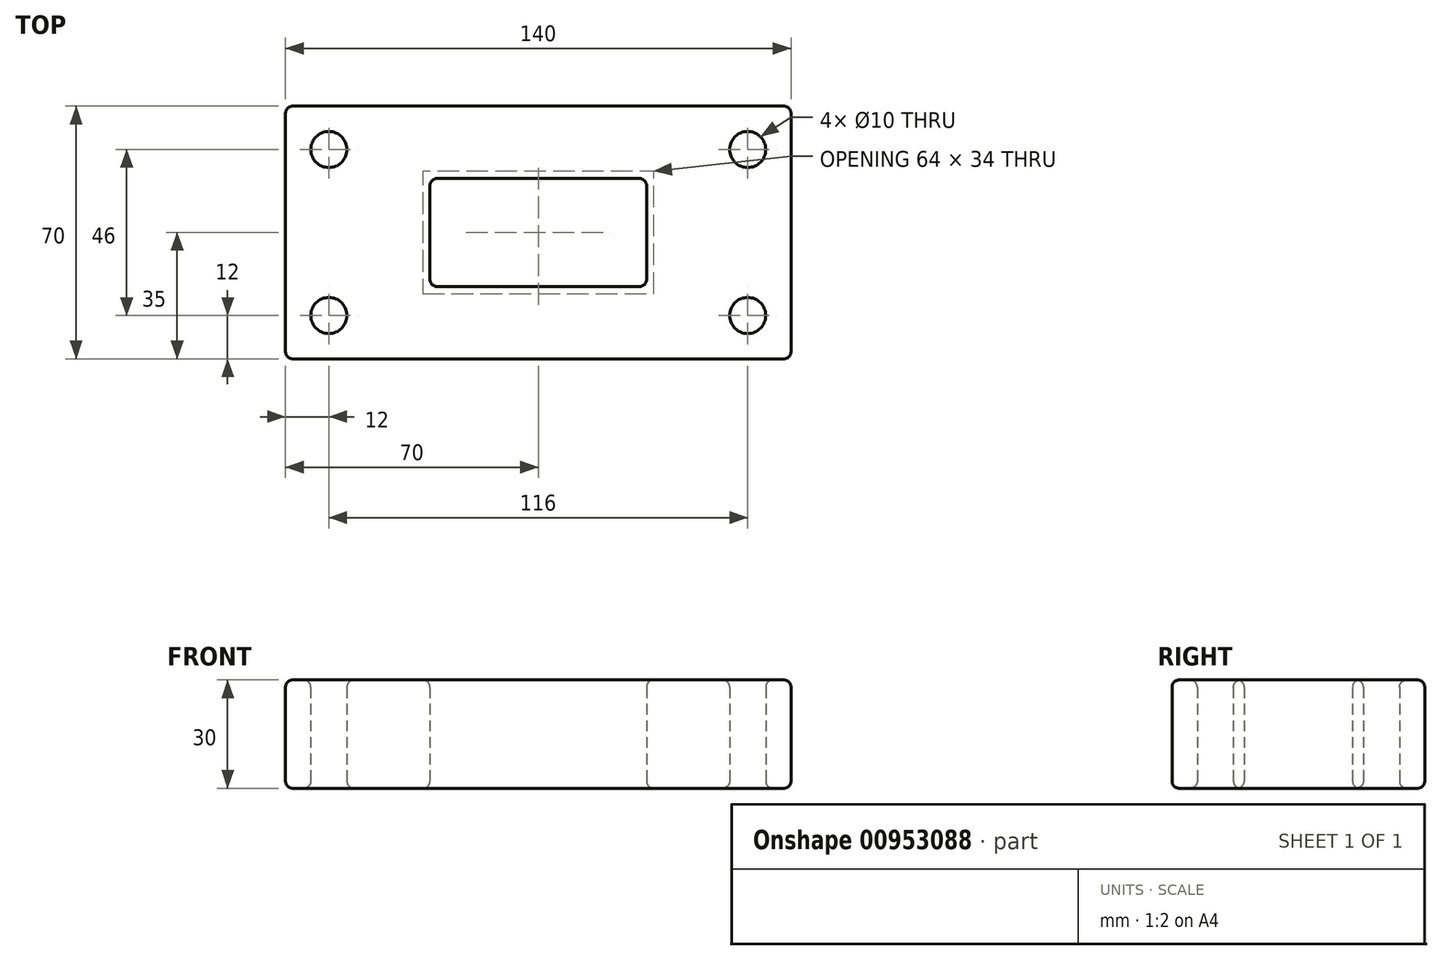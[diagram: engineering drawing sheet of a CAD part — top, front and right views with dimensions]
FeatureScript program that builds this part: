
annotation { "Feature Type Name" : "Feature", "Feature Type Description" : "" }
export const myFeature = defineFeature(function(context is Context, id is Id, definition is map)
    precondition{}
    {
        {
            var Q0;
            Q0=qCreatedBy(makeId("Top.planeOp"),FACE);
            var sketch = newSketch(context, id + "F0", { "sketchPlane" : qUnion([Q0])});
            skLineSegment(sketch, "E0", {"start": v(0, 118.1) * mm, "end": v(0, -115.12) * mm, "construction": true});
            skLineSegment(sketch, "E1", {"start": v(-191.06, 0) * mm, "end": v(202.57, 0) * mm, "construction": true});
            skLineSegment(sketch, "E2.bottom", {"start": v(-70, 35) * mm, "end": v(70, 35) * mm});
            skLineSegment(sketch, "E2.top", {"start": v(-70, -35) * mm, "end": v(70, -35) * mm});
            skLineSegment(sketch, "E2.left", {"start": v(-70, 35) * mm, "end": v(-70, -35) * mm});
            skLineSegment(sketch, "E2.right", {"start": v(70, 35) * mm, "end": v(70, -35) * mm});
            skPoint(sketch, "E2.middle", {"position": v(0, 0) * mm});
            skLineSegment(sketch, "E3.bottom", {"start": v(-30, 15) * mm, "end": v(30, 15) * mm});
            skLineSegment(sketch, "E3.top", {"start": v(-30, -15) * mm, "end": v(30, -15) * mm});
            skLineSegment(sketch, "E3.left", {"start": v(-30, 15) * mm, "end": v(-30, -15) * mm});
            skLineSegment(sketch, "E3.right", {"start": v(30, 15) * mm, "end": v(30, -15) * mm});
            skCircle(sketch, "E4", {"center": v(-58, 23) * mm, "radius": 5 * mm});
            skCircle(sketch, "E5", {"center": v(58, 23) * mm, "radius": 5 * mm});
            skCircle(sketch, "E6.MirrorC", {"center": v(-58, -23) * mm, "radius": 5 * mm});
            skCircle(sketch, "E7.MirrorC", {"center": v(58, -23) * mm, "radius": 5 * mm});
            skSolve(sketch);
        }
        {
            var Q0;
            Q0=makeQuery(id+"F0.imprint","IMPRINT",FACE,{"disambiguationData":[TD([[makeQuery(id+"F0.imprint","IMPRINT",EDGE,{"derivedFrom":sQuery(id+"F0.wireOp",EDGE,"E2.bottom")}),-1.0]])]});
            extrude(context, id + "F1", {"entities" : qUnion([Q0]), "depth" : 30 * mm, "offsetDistance" : 25 * mm});
        }
        {
            var Q0;
            Q0=makeQuery(id+"F1.opExtrude","CAP_FACE",FACE,{"disambiguationData":[OSD([sQuery(id+"F0.wireOp",EDGE,"E2.bottom"),sQuery(id+"F0.wireOp",EDGE,"E2.top"),sQuery(id+"F0.wireOp",EDGE,"E2.left"),sQuery(id+"F0.wireOp",EDGE,"E2.right"),sQuery(id+"F0.wireOp",EDGE,"E3.bottom"),sQuery(id+"F0.wireOp",EDGE,"E3.top"),sQuery(id+"F0.wireOp",EDGE,"E3.left"),sQuery(id+"F0.wireOp",EDGE,"E3.right"),sQuery(id+"F0.wireOp",EDGE,"E4"),sQuery(id+"F0.wireOp",EDGE,"E5"),sQuery(id+"F0.wireOp",EDGE,"E6.MirrorC"),sQuery(id+"F0.wireOp",EDGE,"E7.MirrorC")])],"isStart":false});
            var Q1;
            Q1=makeQuery(id+"F1.opExtrude","SWEPT_FACE",FACE,{"disambiguationData":[OSD([sQuery(id+"F0.wireOp",EDGE,"E2.top")])]});
            var Q2;
            Q2=makeQuery(id+"F1.opExtrude","SWEPT_FACE",FACE,{"disambiguationData":[OSD([sQuery(id+"F0.wireOp",EDGE,"E2.left")])]});
            var Q3;
            Q3=makeQuery(id+"F1.opExtrude","CAP_FACE",FACE,{"disambiguationData":[OSD([sQuery(id+"F0.wireOp",EDGE,"E2.bottom"),sQuery(id+"F0.wireOp",EDGE,"E2.top"),sQuery(id+"F0.wireOp",EDGE,"E2.left"),sQuery(id+"F0.wireOp",EDGE,"E2.right"),sQuery(id+"F0.wireOp",EDGE,"E3.bottom"),sQuery(id+"F0.wireOp",EDGE,"E3.top"),sQuery(id+"F0.wireOp",EDGE,"E3.left"),sQuery(id+"F0.wireOp",EDGE,"E3.right"),sQuery(id+"F0.wireOp",EDGE,"E4"),sQuery(id+"F0.wireOp",EDGE,"E5"),sQuery(id+"F0.wireOp",EDGE,"E6.MirrorC"),sQuery(id+"F0.wireOp",EDGE,"E7.MirrorC")])],"isStart":true});
            var Q4;
            Q4=makeQuery(id+"F1.opExtrude","SWEPT_FACE",FACE,{"disambiguationData":[OSD([sQuery(id+"F0.wireOp",EDGE,"E3.right")])]});
            var Q5;
            Q5=makeQuery(id+"F1.opExtrude","SWEPT_FACE",FACE,{"disambiguationData":[OSD([sQuery(id+"F0.wireOp",EDGE,"E3.top")])]});
            var Q6;
            Q6=makeQuery(id+"F1.opExtrude","SWEPT_FACE",FACE,{"disambiguationData":[OSD([sQuery(id+"F0.wireOp",EDGE,"E3.bottom")])]});
            var Q7;
            Q7=makeQuery(id+"F1.opExtrude","SWEPT_FACE",FACE,{"disambiguationData":[OSD([sQuery(id+"F0.wireOp",EDGE,"E2.bottom")])]});
            fillet(context, id + "F2", {"entities" : qUnion([Q0, Q1, Q2, Q3, Q4, Q5, Q6, Q7]), "radius" : 2 * mm, "tangentPropagation" : true, "allowEdgeOverflow" : false});
        }
    });
